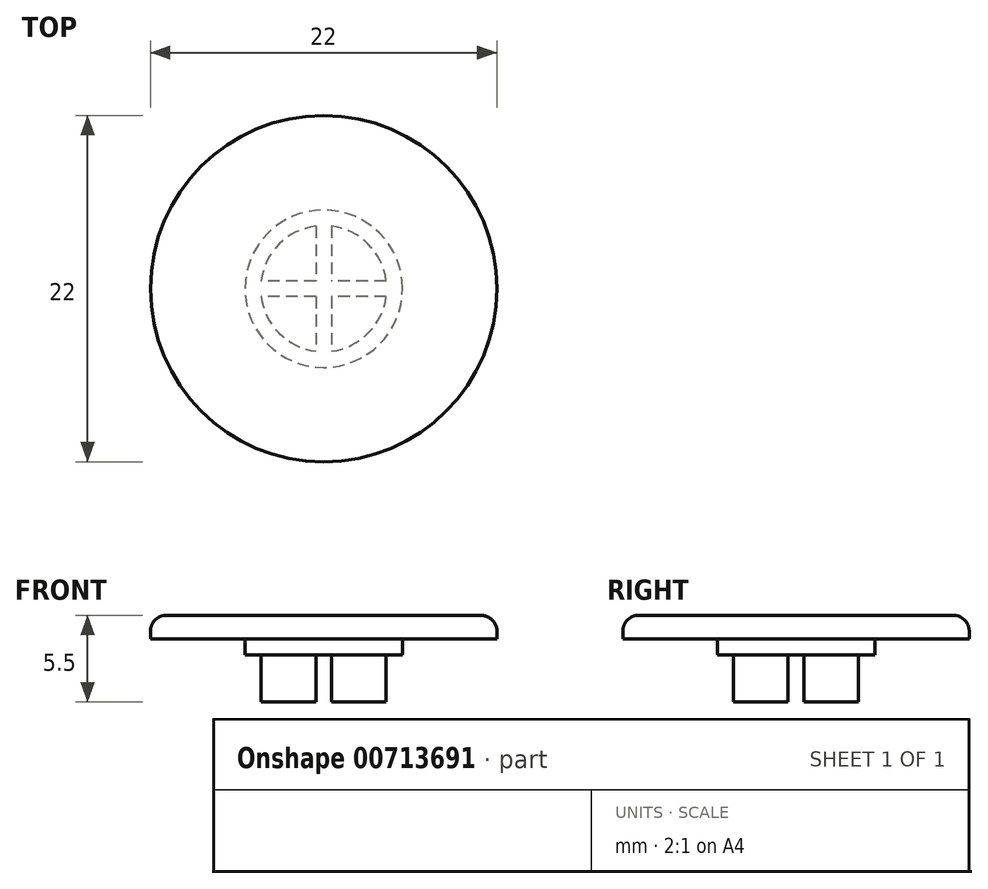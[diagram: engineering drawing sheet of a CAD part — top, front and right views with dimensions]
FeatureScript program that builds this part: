
annotation { "Feature Type Name" : "Feature", "Feature Type Description" : "" }
export const myFeature = defineFeature(function(context is Context, id is Id, definition is map)
    precondition{}
    {
        {
            var Q0;
            Q0=qCreatedBy(makeId("Front.planeOp"),FACE);
            var sketch = newSketch(context, id + "F0", { "sketchPlane" : qUnion([Q0])});
            skLineSegment(sketch, "E0", {"start": v(0, 0) * mm, "end": v(4, 0) * mm});
            skLineSegment(sketch, "E1", {"start": v(4, 0) * mm, "end": v(4, 3) * mm});
            skLineSegment(sketch, "E2", {"start": v(4, 3) * mm, "end": v(5, 3) * mm});
            skLineSegment(sketch, "E3", {"start": v(5, 3) * mm, "end": v(5, 4) * mm});
            skLineSegment(sketch, "E4", {"start": v(5, 4) * mm, "end": v(11, 4) * mm});
            skLineSegment(sketch, "E5", {"start": v(11, 4) * mm, "end": v(11, 5.5) * mm});
            skLineSegment(sketch, "E6", {"start": v(11, 5.5) * mm, "end": v(0, 5.5) * mm});
            skLineSegment(sketch, "E7", {"start": v(0, 5.5) * mm, "end": v(0, 0) * mm});
            skLineSegment(sketch, "E8", {"start": v(0, 0) * mm, "end": v(0, 10.6) * mm, "construction": true});
            skSolve(sketch);
        }
        {
            var Q0;
            Q0 = qSketchRegion(id + "F0", true);
            var Q1;
            Q1=sQuery(id+"F0.wireOp",EDGE,"E8");
            revolve(context, id + "F1", {"surfaceOperationType" : NewSurfaceOperationType.NEW, "entities" : qUnion([Q0]), "axis" : qUnion([Q1]), "revolveType" : RevolveType.FULL});
        }
        {
            var Q0;
            Q0=makeQuery(id+"F1.opRevolve","SWEPT_FACE",FACE,{"disambiguationData":[OSD([sQuery(id+"F0.wireOp",EDGE,"E0")])]});
            var sketch = newSketch(context, id + "F2", { "sketchPlane" : qUnion([Q0])});
            skLineSegment(sketch, "E9.bottom", {"start": v(0.5, -6.4) * mm, "end": v(-0.5, -6.4) * mm});
            skLineSegment(sketch, "E9.top", {"start": v(0.5, 6.4) * mm, "end": v(-0.5, 6.4) * mm});
            skLineSegment(sketch, "E9.left", {"start": v(0.5, -6.4) * mm, "end": v(0.5, -0.5) * mm});
            skLineSegment(sketch, "E9.right", {"start": v(-0.5, -6.4) * mm, "end": v(-0.5, -0.5) * mm});
            skPoint(sketch, "E9.middle", {"position": v(0, 0) * mm});
            skLineSegment(sketch, "E10.bottom", {"start": v(5.62, -0.5) * mm, "end": v(0.5, -0.5) * mm});
            skLineSegment(sketch, "E10.top", {"start": v(5.62, 0.5) * mm, "end": v(0.5, 0.5) * mm});
            skLineSegment(sketch, "E10.left", {"start": v(5.62, -0.5) * mm, "end": v(5.62, 0.5) * mm});
            skLineSegment(sketch, "E10.right", {"start": v(-5.62, -0.5) * mm, "end": v(-5.62, 0.5) * mm});
            skLineSegment(sketch, "E11.trimOffspring", {"start": v(-0.5, 0.5) * mm, "end": v(-5.62, 0.5) * mm});
            skLineSegment(sketch, "E12.trimOffspring", {"start": v(0.5, 0.5) * mm, "end": v(0.5, 6.4) * mm});
            skLineSegment(sketch, "E13.trimOffspring", {"start": v(-0.5, -0.5) * mm, "end": v(-5.62, -0.5) * mm});
            skLineSegment(sketch, "E14.trimOffspring", {"start": v(-0.5, 0.5) * mm, "end": v(-0.5, 6.4) * mm});
            skSolve(sketch);
        }
        {
            var Q0;
            Q0 = qSketchRegion(id + "F2", true);
            var Q1;
            Q1=makeQuery(id+"F1.opRevolve","SWEPT_FACE",FACE,{"disambiguationData":[OSD([sQuery(id+"F0.wireOp",EDGE,"E2")])]});
            extrude(context, id + "F3", {"entities" : qUnion([Q0]), "operationType" : NewBodyOperationType.REMOVE, "endBound" : BoundingType.UP_TO_SURFACE, "oppositeDirection" : true, "depth" : 25 * mm, "endBoundEntityFace" : qUnion([Q1]), "offsetDistance" : 25 * mm});
        }
        {
            var Q0;
            Q0=makeQuery(id+"F1.opRevolve","SWEPT_EDGE",EDGE,{"disambiguationData":[OSD([sQuery(id+"F0.wireOp",EDGE,"E5"),sQuery(id+"F0.wireOp",EDGE,"E6")])]});
            fillet(context, id + "F4", {"entities" : qUnion([Q0]), "radius" : 1 * mm, "tangentPropagation" : true, "allowEdgeOverflow" : false});
        }
    });
